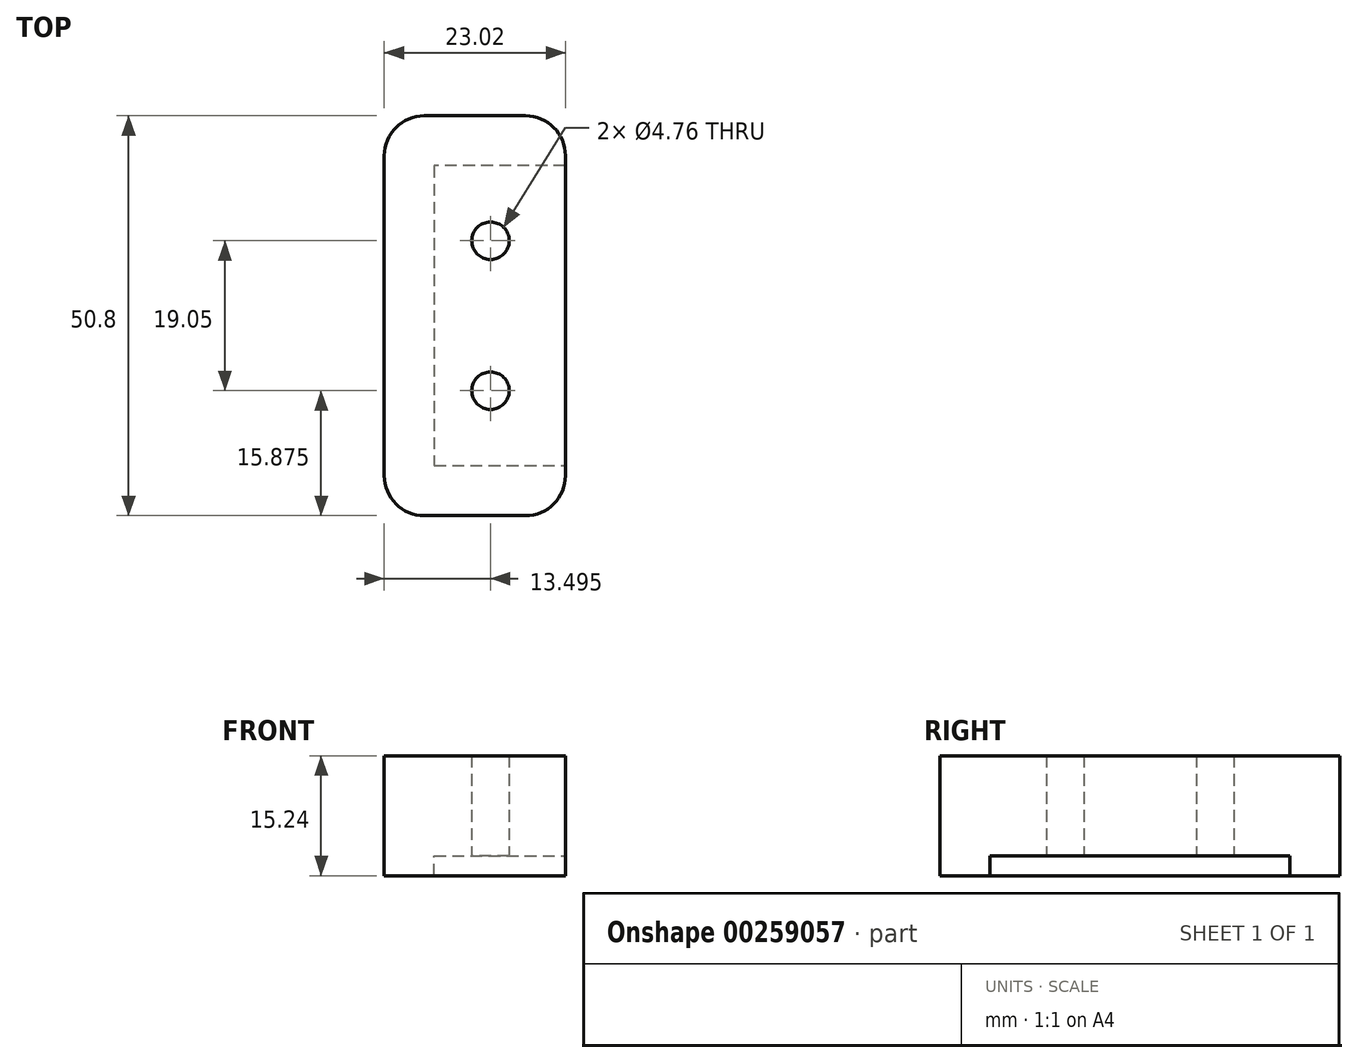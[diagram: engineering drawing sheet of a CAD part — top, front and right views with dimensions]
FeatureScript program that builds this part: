
annotation { "Feature Type Name" : "Feature", "Feature Type Description" : "" }
export const myFeature = defineFeature(function(context is Context, id is Id, definition is map)
    precondition{}
    {
        {
            var Q0;
            Q0=qCreatedBy(makeId("Top.planeOp"),FACE);
            var sketch = newSketch(context, id + "F0", { "sketchPlane" : qUnion([Q0])});
            skLineSegment(sketch, "E0.bottom", {"start": v(-226.22, 38.1) * mm, "end": v(226.22, 38.1) * mm});
            skLineSegment(sketch, "E0.top", {"start": v(-226.22, 0) * mm, "end": v(226.22, 0) * mm});
            skLineSegment(sketch, "E0.left", {"start": v(-226.22, 38.1) * mm, "end": v(-226.22, 0) * mm});
            skLineSegment(sketch, "E0.right", {"start": v(226.22, 38.1) * mm, "end": v(226.22, 0) * mm});
            skLineSegment(sketch, "E1.bottom", {"start": v(-228.6, -119.44) * mm, "end": v(-209.55, -119.44) * mm, "construction": true});
            skLineSegment(sketch, "E1.top", {"start": v(-228.6, 185.36) * mm, "end": v(-209.55, 185.36) * mm, "construction": true});
            skLineSegment(sketch, "E1.left", {"start": v(-228.6, -119.44) * mm, "end": v(-228.6, 185.36) * mm, "construction": true});
            skLineSegment(sketch, "E1.right", {"start": v(-209.55, -119.44) * mm, "end": v(-209.55, 185.36) * mm, "construction": true});
            skLineSegment(sketch, "E2.bottom", {"start": v(209.55, -119.44) * mm, "end": v(228.6, -119.44) * mm, "construction": true});
            skLineSegment(sketch, "E2.top", {"start": v(209.55, 185.36) * mm, "end": v(228.6, 185.36) * mm, "construction": true});
            skLineSegment(sketch, "E2.left", {"start": v(209.55, -119.44) * mm, "end": v(209.55, 185.36) * mm, "construction": true});
            skLineSegment(sketch, "E2.right", {"start": v(228.6, -119.44) * mm, "end": v(228.6, 185.36) * mm, "construction": true});
            skPoint(sketch, "E3", {"position": v(0, 0) * mm});
            skLineSegment(sketch, "E4", {"start": v(-209.55, 185.36) * mm, "end": v(209.55, 185.36) * mm, "construction": true});
            skPoint(sketch, "E5", {"position": v(0, 185.36) * mm});
            skCircle(sketch, "E6", {"center": v(-219.08, 28.57) * mm, "radius": 2.38 * mm});
            skCircle(sketch, "E7", {"center": v(-219.08, 9.52) * mm, "radius": 2.38 * mm});
            skLineSegment(sketch, "E8", {"start": v(-219.08, 28.57) * mm, "end": v(-228.6, 28.57) * mm, "construction": true});
            skLineSegment(sketch, "E9", {"start": v(-228.6, 28.57) * mm, "end": v(-219.08, 28.57) * mm, "construction": true});
            skLineSegment(sketch, "E10", {"start": v(-219.08, 28.57) * mm, "end": v(-209.55, 28.57) * mm, "construction": true});
            skLineSegment(sketch, "E11", {"start": v(-219.07, 28.57) * mm, "end": v(-219.07, 38.1) * mm, "construction": true});
            skLineSegment(sketch, "E12", {"start": v(-219.07, 9.52) * mm, "end": v(-219.07, 0) * mm, "construction": true});
            skLineSegment(sketch, "E13", {"start": v(-219.07, 9.52) * mm, "end": v(-219.07, 19.05) * mm, "construction": true});
            skLineSegment(sketch, "E14", {"start": v(-219.07, 19.05) * mm, "end": v(-219.07, 28.57) * mm, "construction": true});
            skSolve(sketch);
        }
        {
            var Q0;
            Q0=qCreatedBy(makeId("Top.planeOp"),FACE);
            var sketch = newSketch(context, id + "F1", { "sketchPlane" : qUnion([Q0])});
            skLineSegment(sketch, "E15.bottom", {"start": v(-232.57, 44.45) * mm, "end": v(-209.55, 44.45) * mm});
            skLineSegment(sketch, "E15.top", {"start": v(-232.57, -6.35) * mm, "end": v(-209.55, -6.35) * mm});
            skLineSegment(sketch, "E15.left", {"start": v(-232.57, 44.45) * mm, "end": v(-232.57, -6.35) * mm});
            skLineSegment(sketch, "E15.right", {"start": v(-209.55, 44.45) * mm, "end": v(-209.55, -6.35) * mm});
            skCircle(sketch, "E16", {"center": v(-219.08, 28.57) * mm, "radius": 2.38 * mm});
            skCircle(sketch, "E17", {"center": v(-219.08, 9.52) * mm, "radius": 2.38 * mm});
            skSolve(sketch);
        }
        {
            var Q0;
            Q0=makeQuery(id+"F1.imprint","IMPRINT",FACE,{"disambiguationData":[TD([[makeQuery(id+"F1.imprint","IMPRINT",EDGE,{"derivedFrom":sQuery(id+"F1.wireOp",EDGE,"E15.bottom")}),-1.0]])]});
            extrude(context, id + "F2", {"entities" : qUnion([Q0]), "depth" : 12.7 * mm});
        }
        {
            var Q0;
            Q0=makeQuery(id+"F2.opExtrude","CAP_FACE",FACE,{"disambiguationData":[OSD([sQuery(id+"F1.wireOp",EDGE,"E15.bottom"),sQuery(id+"F1.wireOp",EDGE,"E15.top"),sQuery(id+"F1.wireOp",EDGE,"E15.left"),sQuery(id+"F1.wireOp",EDGE,"E15.right"),sQuery(id+"F1.wireOp",EDGE,"E16"),sQuery(id+"F1.wireOp",EDGE,"E17")])],"isStart":true});
            var sketch = newSketch(context, id + "F3", { "sketchPlane" : qUnion([Q0])});
            skLineSegment(sketch, "E18", {"start": v(-232.57, 6.35) * mm, "end": v(-232.57, -44.45) * mm});
            skLineSegment(sketch, "E19", {"start": v(-232.57, -44.45) * mm, "end": v(-209.55, -44.45) * mm});
            skLineSegment(sketch, "E20", {"start": v(-209.55, -44.45) * mm, "end": v(-209.55, -38.1) * mm});
            skLineSegment(sketch, "E21", {"start": v(-209.55, -38.1) * mm, "end": v(-226.22, -38.1) * mm});
            skLineSegment(sketch, "E22", {"start": v(-226.22, -38.1) * mm, "end": v(-226.22, 0) * mm});
            skLineSegment(sketch, "E23", {"start": v(-226.22, 0) * mm, "end": v(-209.55, 0) * mm});
            skLineSegment(sketch, "E24", {"start": v(-209.55, 0) * mm, "end": v(-209.55, 6.35) * mm});
            skLineSegment(sketch, "E25", {"start": v(-209.55, 6.35) * mm, "end": v(-232.57, 6.35) * mm});
            skSolve(sketch);
        }
        {
            var Q0;
            Q0=makeQuery(id+"F3.imprint","IMPRINT",FACE,{"disambiguationData":[TD([[makeQuery(id+"F3.imprint","IMPRINT",EDGE,{"derivedFrom":sQuery(id+"F3.wireOp",EDGE,"E18")}),-1.0]])]});
            extrude(context, id + "F4", {"entities" : qUnion([Q0]), "operationType" : NewBodyOperationType.ADD, "depth" : 2.54 * mm});
        }
        {
            var Q0;
            Q0=makeQuery(id+"F4.boolean.opBoolean","MERGE",EDGE,{"derivedFrom":[makeQuery(id+"F2.opExtrude","SWEPT_EDGE",EDGE,{"disambiguationData":[OSD([sQuery(id+"F1.wireOp",EDGE,"E15.top"),sQuery(id+"F1.wireOp",EDGE,"E15.right")])]}),makeQuery(id+"F4.opExtrude","SWEPT_EDGE",EDGE,{"disambiguationData":[OSD([sQuery(id+"F3.wireOp",EDGE,"E24"),sQuery(id+"F3.wireOp",EDGE,"E25")])]})]});
            var Q1;
            Q1=makeQuery(id+"F4.boolean.opBoolean","MERGE",EDGE,{"derivedFrom":[makeQuery(id+"F2.opExtrude","SWEPT_EDGE",EDGE,{"disambiguationData":[OSD([sQuery(id+"F1.wireOp",EDGE,"E15.top"),sQuery(id+"F1.wireOp",EDGE,"E15.left")])]}),makeQuery(id+"F4.opExtrude","SWEPT_EDGE",EDGE,{"disambiguationData":[OSD([sQuery(id+"F3.wireOp",EDGE,"E18"),sQuery(id+"F3.wireOp",EDGE,"E25")])]})]});
            var Q2;
            Q2=makeQuery(id+"F4.boolean.opBoolean","MERGE",EDGE,{"derivedFrom":[makeQuery(id+"F2.opExtrude","SWEPT_EDGE",EDGE,{"disambiguationData":[OSD([sQuery(id+"F1.wireOp",EDGE,"E15.bottom"),sQuery(id+"F1.wireOp",EDGE,"E15.left")])]}),makeQuery(id+"F4.opExtrude","SWEPT_EDGE",EDGE,{"disambiguationData":[OSD([sQuery(id+"F3.wireOp",EDGE,"E18"),sQuery(id+"F3.wireOp",EDGE,"E19")])]})]});
            var Q3;
            Q3=makeQuery(id+"F4.boolean.opBoolean","MERGE",EDGE,{"derivedFrom":[makeQuery(id+"F2.opExtrude","SWEPT_EDGE",EDGE,{"disambiguationData":[OSD([sQuery(id+"F1.wireOp",EDGE,"E15.bottom"),sQuery(id+"F1.wireOp",EDGE,"E15.right")])]}),makeQuery(id+"F4.opExtrude","SWEPT_EDGE",EDGE,{"disambiguationData":[OSD([sQuery(id+"F3.wireOp",EDGE,"E19"),sQuery(id+"F3.wireOp",EDGE,"E20")])]})]});
            fillet(context, id + "F5", {"entities" : qUnion([Q0, Q1, Q2, Q3]), "radius" : 5.08 * mm, "tangentPropagation" : true, "allowEdgeOverflow" : false});
        }
    });
